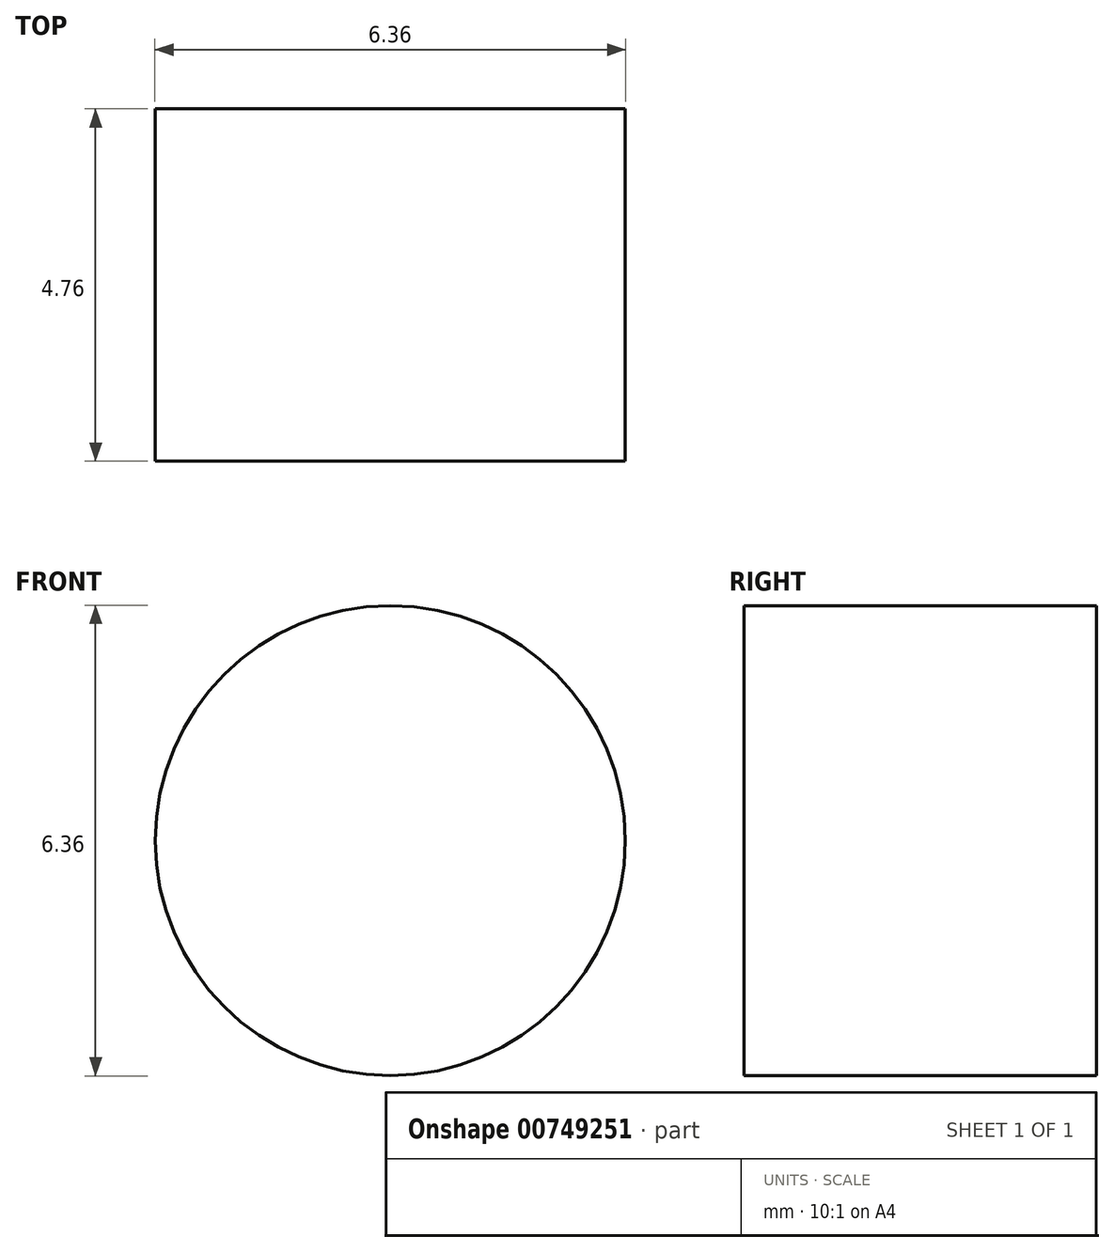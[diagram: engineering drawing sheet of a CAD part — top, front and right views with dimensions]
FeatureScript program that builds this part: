
annotation { "Feature Type Name" : "Feature", "Feature Type Description" : "" }
export const myFeature = defineFeature(function(context is Context, id is Id, definition is map)
    precondition{}
    {
        {
            var Q0;
            Q0=qCreatedBy(makeId("Front.planeOp"),FACE);
            var sketch = newSketch(context, id + "F0", { "sketchPlane" : qUnion([Q0])});
            skCircle(sketch, "E0", {"center": v(0, 0) * mm, "radius": 3.18 * mm});
            skSolve(sketch);
        }
        {
            var Q0;
            Q0 = qSketchRegion(id + "F0", true);
            extrude(context, id + "F1", {"entities" : qUnion([Q0]), "depth" : 4.76 * mm, "offsetDistance" : 25.4 * mm});
        }
    });
